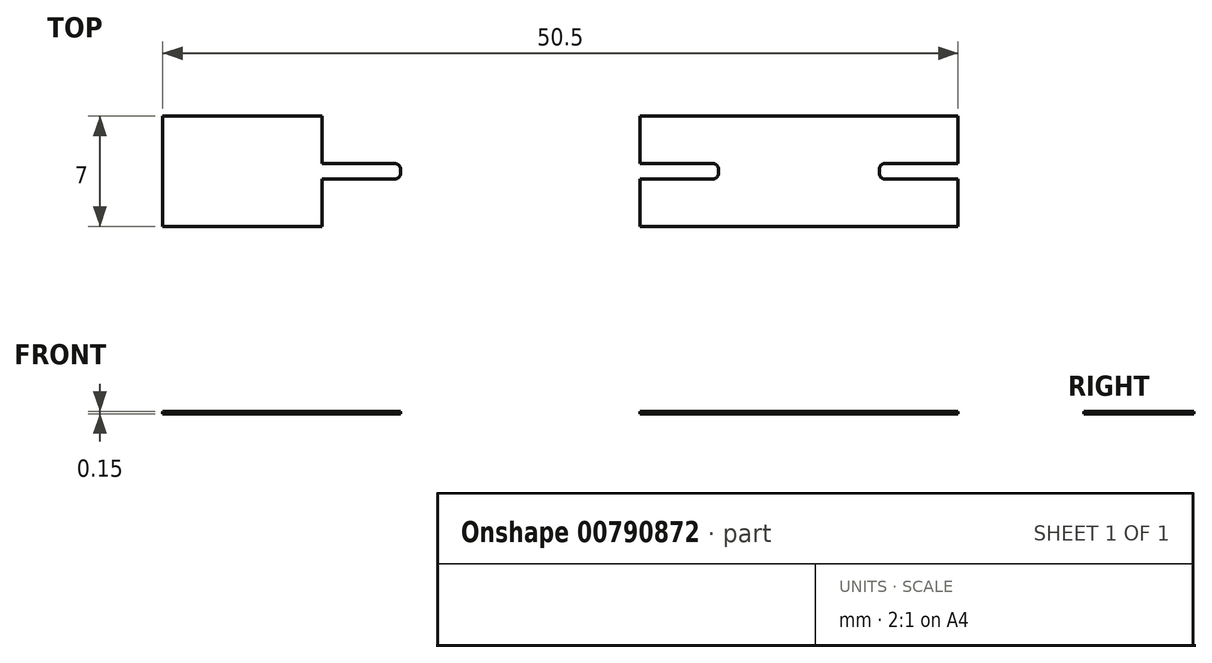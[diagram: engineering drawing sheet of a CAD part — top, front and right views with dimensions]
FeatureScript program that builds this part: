
annotation { "Feature Type Name" : "Feature", "Feature Type Description" : "" }
export const myFeature = defineFeature(function(context is Context, id is Id, definition is map)
    precondition{}
    {
        {
            var Q0;
            Q0=qCreatedBy(makeId("Top.planeOp"),FACE);
            var sketch = newSketch(context, id + "F0", { "sketchPlane" : qUnion([Q0])});
            skPoint(sketch, "E0.middle", {"position": v(0, 0) * mm});
            skLineSegment(sketch, "E1.bottom", {"start": v(-5.5, -0.5) * mm, "end": v(-10.1, -0.5) * mm});
            skLineSegment(sketch, "E1.top", {"start": v(-5.5, 0.5) * mm, "end": v(-10.1, 0.5) * mm});
            skLineSegment(sketch, "E1.left", {"start": v(-5.1, -0.1) * mm, "end": v(-5.1, 0.1) * mm});
            skLineSegment(sketch, "E1.right", {"start": v(-15.1, -0.1) * mm, "end": v(-15.1, 0.1) * mm});
            skPoint(sketch, "E1.middle", {"position": v(-10.1, 0) * mm});
            skPoint(sketch, "E2.visualSharp", {"position": v(-5.1, 0.5) * mm});
            skArc(sketch, "E2.filletArc", {"start": v(-5.1, 0.1) * mm, "mid": v(-5.22, 0.38) * mm, "end": v(-5.5, 0.5) * mm});
            skPoint(sketch, "E3.visualSharp", {"position": v(-5.1, -0.5) * mm});
            skArc(sketch, "E3.filletArc", {"start": v(-5.5, -0.5) * mm, "mid": v(-5.22, -0.38) * mm, "end": v(-5.1, -0.1) * mm});
            skPoint(sketch, "E4.visualSharp", {"position": v(-15.1, 0.5) * mm});
            skArc(sketch, "E4.filletArc", {"start": v(-14.7, 0.5) * mm, "mid": v(-14.98, 0.38) * mm, "end": v(-15.1, 0.1) * mm});
            skPoint(sketch, "E5.visualSharp", {"position": v(-15.1, -0.5) * mm});
            skArc(sketch, "E5.filletArc", {"start": v(-15.1, -0.1) * mm, "mid": v(-14.98, -0.38) * mm, "end": v(-14.7, -0.5) * mm});
            skLineSegment(sketch, "E6", {"start": v(0, 3.5) * mm, "end": v(-10.1, 3.5) * mm});
            skPoint(sketch, "E6.endSnap0", {"position": v(-10.1, 0.5) * mm});
            skLineSegment(sketch, "E7", {"start": v(-10.1, 3.5) * mm, "end": v(-10.1, 0.5) * mm});
            skLineSegment(sketch, "E8.MirrorCS", {"start": v(0, -3.5) * mm, "end": v(-10.1, -3.5) * mm});
            skLineSegment(sketch, "E9.MirrorCS", {"start": v(-10.1, -3.5) * mm, "end": v(-10.1, -0.5) * mm});
            skLineSegment(sketch, "E10.MirrorCS", {"start": v(0, 3.5) * mm, "end": v(10.1, 3.5) * mm});
            skLineSegment(sketch, "E11.MirrorCS", {"start": v(0, -3.5) * mm, "end": v(10.1, -3.5) * mm});
            skLineSegment(sketch, "E12.MirrorCS", {"start": v(5.1, -0.1) * mm, "end": v(5.1, 0.1) * mm});
            skArc(sketch, "E13.MirrorCS", {"start": v(5.1, 0.1) * mm, "mid": v(5.22, 0.38) * mm, "end": v(5.5, 0.5) * mm});
            skArc(sketch, "E14.MirrorCS", {"start": v(15.1, -0.1) * mm, "mid": v(14.98, -0.38) * mm, "end": v(14.7, -0.5) * mm});
            skLineSegment(sketch, "E15.MirrorCS", {"start": v(15.1, -0.1) * mm, "end": v(15.1, 0.1) * mm});
            skArc(sketch, "E16.MirrorCS", {"start": v(14.7, 0.5) * mm, "mid": v(14.98, 0.38) * mm, "end": v(15.1, 0.1) * mm});
            skArc(sketch, "E17.MirrorCS", {"start": v(5.5, -0.5) * mm, "mid": v(5.22, -0.38) * mm, "end": v(5.1, -0.1) * mm});
            skPoint(sketch, "E18.MirrorP", {"position": v(15.1, 0.5) * mm});
            skLineSegment(sketch, "E19.MirrorCS", {"start": v(5.5, 0.5) * mm, "end": v(14.7, 0.5) * mm});
            skLineSegment(sketch, "E20.MirrorCS", {"start": v(5.5, -0.5) * mm, "end": v(14.7, -0.5) * mm});
            skPoint(sketch, "E21.MirrorP", {"position": v(10.1, 0.5) * mm});
            skPoint(sketch, "E22.MirrorP", {"position": v(5.1, 0.5) * mm});
            skPoint(sketch, "E23.MirrorP", {"position": v(15.1, -0.5) * mm});
            skPoint(sketch, "E24.MirrorP", {"position": v(5.1, -0.5) * mm});
            skPoint(sketch, "E25.MirrorP", {"position": v(10.1, 0) * mm});
            skLineSegment(sketch, "E26.MirrorCS", {"start": v(10.1, 3.5) * mm, "end": v(10.1, 0.5) * mm});
            skLineSegment(sketch, "E27.MirrorCS", {"start": v(10.1, -3.5) * mm, "end": v(10.1, -0.5) * mm});
            skPoint(sketch, "E28.1.0.0", {"position": v(25.3, 0.5) * mm});
            skLineSegment(sketch, "E28.1.0.1", {"start": v(20.2, 3.5) * mm, "end": v(30.3, 3.5) * mm});
            skLineSegment(sketch, "E28.1.0.2", {"start": v(25.7, -0.5) * mm, "end": v(34.9, -0.5) * mm});
            skPoint(sketch, "E28.1.0.3", {"position": v(20.2, 0) * mm});
            skLineSegment(sketch, "E28.1.0.4", {"start": v(20.2, -3.5) * mm, "end": v(30.3, -3.5) * mm});
            skPoint(sketch, "E28.1.0.5", {"position": v(30.3, 0.5) * mm});
            skPoint(sketch, "E28.1.0.6", {"position": v(30.3, 0) * mm});
            skPoint(sketch, "E28.1.0.7", {"position": v(35.3, -0.5) * mm});
            skPoint(sketch, "E28.1.0.8", {"position": v(25.3, -0.5) * mm});
            skLineSegment(sketch, "E28.1.0.9", {"start": v(20.2, -3.5) * mm, "end": v(10.1, -3.5) * mm});
            skLineSegment(sketch, "E28.1.0.10", {"start": v(25.7, 0.5) * mm, "end": v(34.9, 0.5) * mm});
            skLineSegment(sketch, "E28.1.0.11", {"start": v(20.2, 3.5) * mm, "end": v(10.1, 3.5) * mm});
            skLineSegment(sketch, "E28.1.0.12", {"start": v(30.3, 3.5) * mm, "end": v(30.3, 0.5) * mm});
            skLineSegment(sketch, "E28.1.0.13", {"start": v(30.3, -3.5) * mm, "end": v(30.3, -0.5) * mm});
            skPoint(sketch, "E28.1.0.14", {"position": v(35.3, 0.5) * mm});
            skArc(sketch, "E28.1.0.15", {"start": v(34.9, 0.5) * mm, "mid": v(35.18, 0.38) * mm, "end": v(35.3, 0.1) * mm});
            skArc(sketch, "E28.1.0.16", {"start": v(25.7, -0.5) * mm, "mid": v(25.42, -0.38) * mm, "end": v(25.3, -0.1) * mm});
            skArc(sketch, "E28.1.0.17", {"start": v(35.3, -0.1) * mm, "mid": v(35.18, -0.38) * mm, "end": v(34.9, -0.5) * mm});
            skArc(sketch, "E28.1.0.18", {"start": v(25.3, 0.1) * mm, "mid": v(25.42, 0.38) * mm, "end": v(25.7, 0.5) * mm});
            skLineSegment(sketch, "E28.1.0.19", {"start": v(25.3, -0.1) * mm, "end": v(25.3, 0.1) * mm});
            skLineSegment(sketch, "E28.1.0.20", {"start": v(35.3, -0.1) * mm, "end": v(35.3, 0.1) * mm});
            skLineSegment(sketch, "E28.direction1", {"start": v(-10.1, -3.5) * mm, "end": v(10.1, -3.5) * mm, "construction": true});
            skLineSegment(sketch, "E29", {"start": v(0, 3.5) * mm, "end": v(0, -3.5) * mm});
            skPoint(sketch, "E30.0.2.0", {"position": v(45.5, 0.5) * mm});
            skLineSegment(sketch, "E30.1.2.0", {"start": v(40.4, 3.5) * mm, "end": v(50.5, 3.5) * mm});
            skLineSegment(sketch, "E30.4.2.0", {"start": v(45.9, -0.5) * mm, "end": v(55.1, -0.5) * mm});
            skPoint(sketch, "E30.7.2.0", {"position": v(40.4, 0) * mm});
            skLineSegment(sketch, "E30.8.2.0", {"start": v(40.4, -3.5) * mm, "end": v(50.5, -3.5) * mm});
            skPoint(sketch, "E30.11.2.0", {"position": v(50.5, 0.5) * mm});
            skPoint(sketch, "E30.12.2.0", {"position": v(50.5, 0) * mm});
            skPoint(sketch, "E30.13.2.0", {"position": v(55.5, -0.5) * mm});
            skPoint(sketch, "E30.14.2.0", {"position": v(45.5, -0.5) * mm});
            skLineSegment(sketch, "E30.15.2.0", {"start": v(40.4, -3.5) * mm, "end": v(30.3, -3.5) * mm});
            skLineSegment(sketch, "E30.18.2.0", {"start": v(45.9, 0.5) * mm, "end": v(55.1, 0.5) * mm});
            skLineSegment(sketch, "E30.21.2.0", {"start": v(40.4, 3.5) * mm, "end": v(30.3, 3.5) * mm});
            skLineSegment(sketch, "E30.24.2.0", {"start": v(50.5, 3.5) * mm, "end": v(50.5, 0.5) * mm});
            skLineSegment(sketch, "E30.27.2.0", {"start": v(50.5, -3.5) * mm, "end": v(50.5, -0.5) * mm});
            skPoint(sketch, "E30.30.2.0", {"position": v(55.5, 0.5) * mm});
            skArc(sketch, "E30.31.2.0", {"start": v(55.1, 0.5) * mm, "mid": v(55.38, 0.38) * mm, "end": v(55.5, 0.1) * mm});
            skArc(sketch, "E30.35.2.0", {"start": v(45.9, -0.5) * mm, "mid": v(45.62, -0.38) * mm, "end": v(45.5, -0.1) * mm});
            skArc(sketch, "E30.39.2.0", {"start": v(55.5, -0.1) * mm, "mid": v(55.38, -0.38) * mm, "end": v(55.1, -0.5) * mm});
            skArc(sketch, "E30.43.2.0", {"start": v(45.5, 0.1) * mm, "mid": v(45.62, 0.38) * mm, "end": v(45.9, 0.5) * mm});
            skLineSegment(sketch, "E30.47.2.0", {"start": v(45.5, -0.1) * mm, "end": v(45.5, 0.1) * mm});
            skLineSegment(sketch, "E30.50.2.0", {"start": v(55.5, -0.1) * mm, "end": v(55.5, 0.1) * mm});
            skSolve(sketch);
        }
        {
            var Q0;
            {var subQ8=sQuery(id+"F0.wireOp",EDGE,"E28.3.0.12");Q0=makeQuery(id+"F0.imprint","IMPRINT",FACE,{"disambiguationData":[TD([[makeQuery(id+"F0.imprint","IMPRINT",EDGE,{"derivedFrom":subQ8}),1.0]])]});}
            var Q1;
            {var subQ3=sQuery(id+"F0.wireOp",EDGE,"E14.MirrorCS");Q1=makeQuery(id+"F0.imprint","IMPRINT",FACE,{"disambiguationData":[TD([[makeQuery(id+"F0.imprint","IMPRINT",EDGE,{"derivedFrom":subQ3}),1.0]])]});}
            var Q2;
            {var subQ8=sQuery(id+"F0.wireOp",EDGE,"E28.1.0.12");Q2=makeQuery(id+"F0.imprint","IMPRINT",FACE,{"disambiguationData":[TD([[makeQuery(id+"F0.imprint","IMPRINT",EDGE,{"derivedFrom":subQ8}),1.0]])]});}
            var Q3;
            {var subQ8=sQuery(id+"F0.wireOp",EDGE,"E28.2.0.12");Q3=makeQuery(id+"F0.imprint","IMPRINT",FACE,{"disambiguationData":[TD([[makeQuery(id+"F0.imprint","IMPRINT",EDGE,{"derivedFrom":subQ8}),1.0]])]});}
            var Q4;
            Q4=makeQuery(id+"F0.imprint","IMPRINT",FACE,{"disambiguationData":[TD([[makeQuery(id+"F0.imprint","IMPRINT",EDGE,{"derivedFrom":sQuery(id+"F0.wireOp",EDGE,"E10.MirrorCS")}),-1.0]])]});
            extrude(context, id + "F1", {"entities" : qUnion([Q0, Q1, Q2, Q3, Q4]), "depth" : 0.15 * mm, "offsetDistance" : 25 * mm});
        }
    });
